# Revit family: P300255-031
name_source: partatom
category: Lighting Fixtures
revit_build: Autodesk Revit 2014 (Build: 20130308_1515(x64)
units: mm (PartAtom-declared; Revit-internal decimal feet)

## types (1)
- P300255-031
    Apparent Load = 60 VA
    Assembly Code = D5020200
    Connector Description = Lighting Connector
    Default Elevation = 48"
    Description = Beautiful lighting will appeal to both your classic taste and your artistic spirit
with this bath light. Wandering eyes will focus on clear chiseled glass shades
as they offer an air of refinery. Handsome black light bases are supported by
dainty curved arms to complete the elegant design.
    Fixture distribution = Direct
    Glass = Hubbell - Glass
    Gold = Hubbell - Gold
    Housing Material = Paint - Hubbell - Textured Camera Black
    Lamp = Medium Base or LED
    Load Classification = Lighting
    Manufacturer = Progress Lighting
    Model = P300255-031
    Power Factor = 1
    Product Documentation Link = https://hubbellcdn.com
    Product Link = https://www.hubbell.com
    Specifications = Wandering eyes will focus on clear chiseled glass shades as they offer an air of refinery.
• Handsome black light bases are supported by dainty curved arms to complete the elegant
design.
• Beautiful lighting will appeal to both your classic taste and your artistic spirit with this bath
light.
• Ideal for any bathroom.
• Perfect for transitional, rustic, farmhouse, or coastal settings.
• Measures 25-inch width by 7-3/4-inch height.
• Uses three medium base bulbs that are sold separately (60w max - LED or incandescent).
• Able to be fully dimmable with dimmable bulbs.
• Includes installation instructions and mounting hardware.
• Progress Lighting products are designed for exceptional quality, reliability, and functionality
    URL = https://www.hubbell.com
    Voltage = 120 V
    Warranty = 5 years Warranty
    Wattage Comments = 60W
    Watts = 60 W
    White = Paint - Hubbell - Matte White

## geometry (parser evidence)
native form markers: Sweep x2
no freeform markers — native parametric forms only
